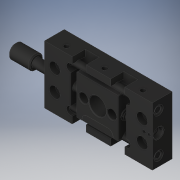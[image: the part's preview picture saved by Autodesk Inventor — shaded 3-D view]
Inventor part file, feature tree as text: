
AUTODESK INVENTOR PART (.ipt)
format: ipt  version: 2019 (Build 230136000, 136)  size: 1,040,896 bytes
history: native  units: in
note: dims shown in document units (in); Inventor stores cm internally (conversion verified against a paired STEP export)
features: plane x2, imported_body x1
ambient origin geometry x8: Origin, YZ Plane, XZ Plane, XY Plane, X Axis, Y Axis, Z Axis, Center Point
bodies: Solid1 (feature_tree)
feature tree (3):
  plane  "Work Plane1"
  plane  "Work Plane2"
  imported_body  "Base1"
